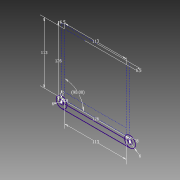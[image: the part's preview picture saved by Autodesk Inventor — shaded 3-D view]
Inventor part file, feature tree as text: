
AUTODESK INVENTOR PART (.ipt)
format: ipt  version: 2014 SP1 (Build 180222100, 222)  size: 74,240 bytes
history: native  units: in
note: dims shown in document units (in); Inventor stores cm internally (conversion verified against a paired STEP export)
features: sketch x1
ambient origin geometry x8: Origin, YZ Plane, XZ Plane, XY Plane, X Axis, Y Axis, Z Axis, Center Point
feature tree (1):
  sketch  "Sketch1"  dims[d0=4.9606in d1=0.315in d2=0.315in d3=0.2362in d4=0.2362in d5=4.9606in d6=4.4488in d7=0.2559in d8=0.2559in d9=4.4488in d11=4.4488in d12=90.0deg d13=0.4724in]
